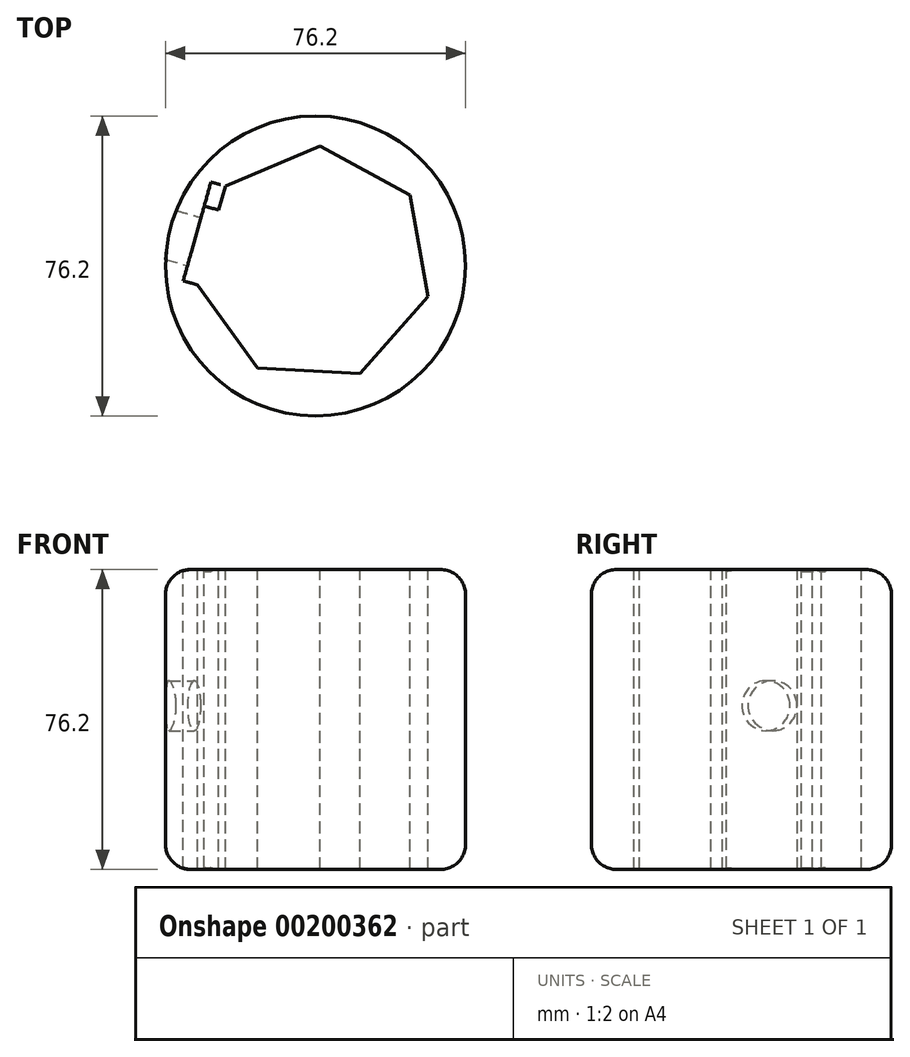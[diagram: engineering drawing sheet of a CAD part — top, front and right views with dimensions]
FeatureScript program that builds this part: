
annotation { "Feature Type Name" : "Feature", "Feature Type Description" : "" }
export const myFeature = defineFeature(function(context is Context, id is Id, definition is map)
    precondition{}
    {
        {
            var Q0;
            Q0=qCreatedBy(makeId("Top.planeOp"),FACE);
            var sketch = newSketch(context, id + "F0", { "sketchPlane" : qUnion([Q0])});
            skCircle(sketch, "E0", {"center": v(0, 0) * mm, "radius": 38.1 * mm});
            skSolve(sketch);
        }
        {
            var Q0;
            Q0=makeQuery(id+"F0.imprint","IMPRINT",FACE,{"disambiguationData":[TD([[makeQuery(id+"F0.imprint","IMPRINT",EDGE,{"derivedFrom":sQuery(id+"F0.wireOp",EDGE,"E0")}),1.0]])]});
            var Q1;
            Q1=sQuery(id+"F0.wireOp",EDGE,"E0");
            extrude(context, id + "F1", {"entities" : qUnion([Q0]), "surfaceEntities" : qUnion([Q1]), "depth" : 76.2 * mm});
        }
        {
            var Q0;
            Q0=makeQuery(id+"F1.opExtrude","CAP_FACE",FACE,{"disambiguationData":[OSD([sQuery(id+"F0.wireOp",EDGE,"E0")])],"isStart":false});
            var sketch = newSketch(context, id + "F2", { "sketchPlane" : qUnion([Q0])});
            skCircle(sketch, "E1.cCircle", {"center": v(-0.36, 0.44) * mm, "radius": 27.08 * mm, "construction": true});
            skLineSegment(sketch, "E1.0", {"start": v(-29.96, -4.8) * mm, "end": v(-22.9, 20.32) * mm});
            skLineSegment(sketch, "E1.1", {"start": v(-22.9, 20.32) * mm, "end": v(1.13, 30.46) * mm});
            skLineSegment(sketch, "E1.2", {"start": v(1.13, 30.46) * mm, "end": v(24.04, 18) * mm});
            skLineSegment(sketch, "E1.3", {"start": v(24.04, 18) * mm, "end": v(28.59, -7.7) * mm});
            skLineSegment(sketch, "E1.4", {"start": v(28.59, -7.7) * mm, "end": v(11.33, -27.26) * mm});
            skLineSegment(sketch, "E1.5", {"start": v(11.33, -27.26) * mm, "end": v(-14.72, -25.97) * mm});
            skLineSegment(sketch, "E1.6", {"start": v(-14.72, -25.97) * mm, "end": v(-29.96, -4.8) * mm});
            skPoint(sketch, "E1.0.midPoint", {"position": v(-26.43, 7.76) * mm});
            skSolve(sketch);
        }
        {
            var Q0;
            Q0=makeQuery(id+"F2.imprint","IMPRINT",FACE,{"disambiguationData":[TD([[makeQuery(id+"F2.imprint","IMPRINT",EDGE,{"derivedFrom":sQuery(id+"F2.wireOp",EDGE,"E1.0")}),-1.0]])]});
            extrude(context, id + "F3", {"entities" : qUnion([Q0]), "operationType" : NewBodyOperationType.REMOVE, "oppositeDirection" : true, "depth" : 76.2 * mm});
        }
        {
            var Q0;
            Q0=makeQuery(id+"F1.opExtrude","SWEPT_FACE",FACE,{"disambiguationData":[OSD([sQuery(id+"F0.wireOp",EDGE,"E0")])]});
            fillet(context, id + "F4", {"entities" : qUnion([Q0]), "radius" : 6.35 * mm, "tangentPropagation" : true, "allowEdgeOverflow" : false});
        }
        {
            var Q0;
            Q0=makeQuery(id+"F3.boolean.opBoolean","COPY",FACE,{"derivedFrom":makeQuery(id+"F3.opExtrude","SWEPT_FACE",FACE,{"disambiguationData":[OSD([sQuery(id+"F2.wireOp",EDGE,"E1.0")])]})});
            extrude(context, id + "F5", {"entities" : qUnion([Q0]), "operationType" : NewBodyOperationType.REMOVE, "oppositeDirection" : true, "depth" : 3.8 * mm});
        }
        {
            var Q0;
            Q0=makeQuery(id+"F5.boolean.opBoolean","COPY",FACE,{"derivedFrom":makeQuery(id+"F5.opExtrude","SWEPT_FACE",FACE,{"disambiguationData":[OSD([sQuery(id+"F2.wireOp",EDGE,"E1.0"),sQuery(id+"F2.wireOp",EDGE,"E1.1")])]})});
            extrude(context, id + "F6", {"entities" : qUnion([Q0]), "operationType" : NewBodyOperationType.ADD, "depth" : 6.35 * mm});
        }
        {
            var Q0;
            Q0=makeQuery(id+"F5.boolean.opBoolean","COPY",FACE,{"derivedFrom":makeQuery(id+"F5.opExtrude","CAP_FACE",FACE,{"disambiguationData":[OSD([sQuery(id+"F2.wireOp",EDGE,"E1.0")])],"isStart":false})});
            var sketch = newSketch(context, id + "F7", { "sketchPlane" : qUnion([Q0])});
            skCircle(sketch, "E2", {"center": v(-2.36, 41.6) * mm, "radius": 6.35 * mm});
            skSolve(sketch);
        }
        {
            var Q0;
            Q0 = qSketchRegion(id + "F7", true);
            extrude(context, id + "F8", {"entities" : qUnion([Q0]), "operationType" : NewBodyOperationType.REMOVE, "oppositeDirection" : true, "depth" : 12.7 * mm});
        }
        {
            var Q0;
            Q0=sQuery(id+"F7.wireOp",EDGE,"E2");
            extrude(context, id + "F9", {"bodyType" : ToolBodyType.SURFACE, "surfaceEntities" : qUnion([Q0]), "depth" : 127 * mm});
        }
    });
